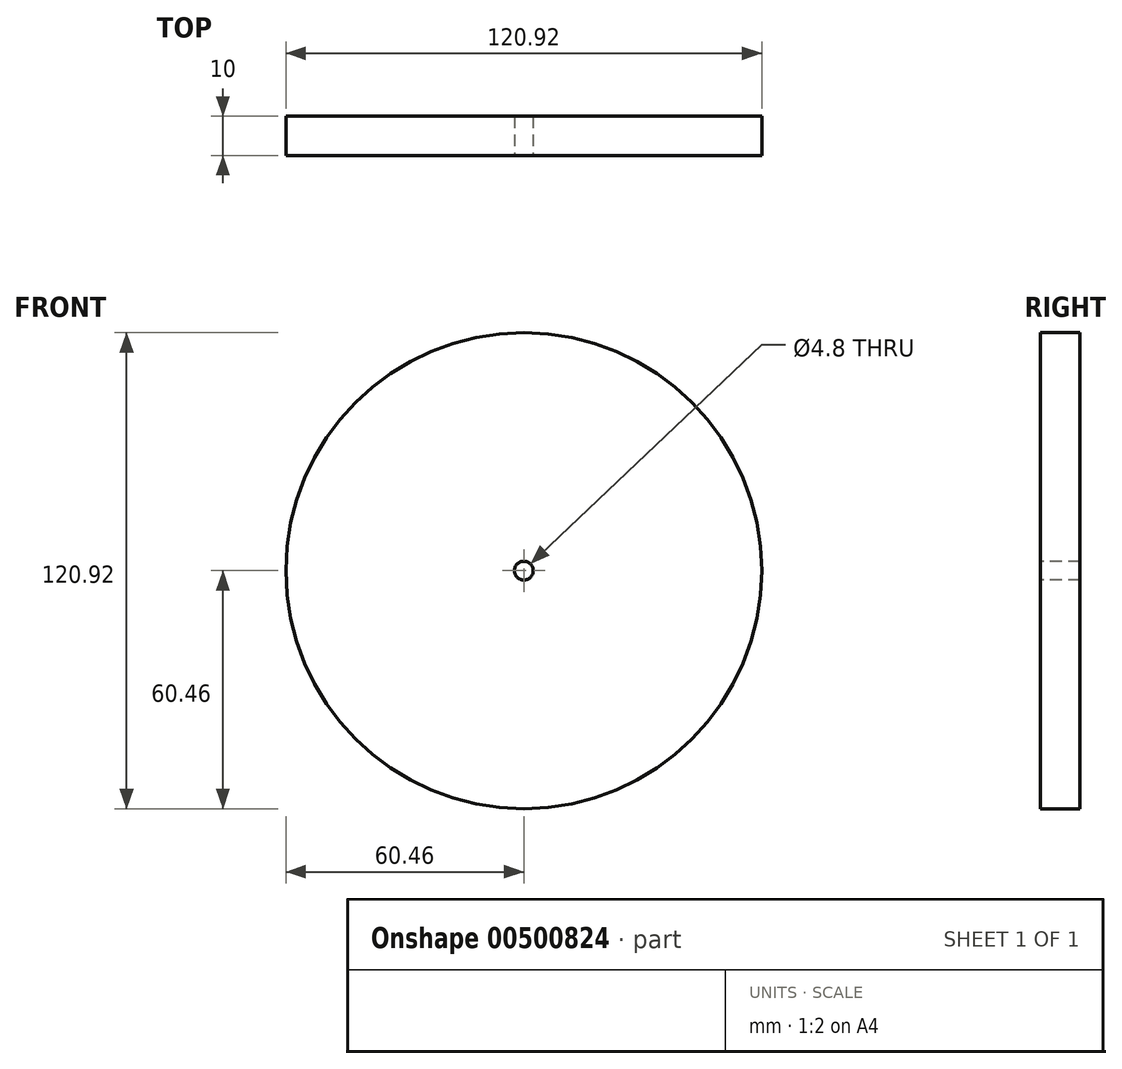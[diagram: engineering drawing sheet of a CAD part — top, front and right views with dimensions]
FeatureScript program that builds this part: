
annotation { "Feature Type Name" : "Feature", "Feature Type Description" : "" }
export const myFeature = defineFeature(function(context is Context, id is Id, definition is map)
    precondition{}
    {
        {
            var Q0;
            Q0=qCreatedBy(makeId("Front.planeOp"),FACE);
            var sketch = newSketch(context, id + "F0", { "sketchPlane" : qUnion([Q0])});
            skCircle(sketch, "E0", {"center": v(0, 0) * mm, "radius": 60.46 * mm});
            skSolve(sketch);
        }
        {
            var Q0;
            Q0=makeQuery(id+"F0.imprint","IMPRINT",FACE,{"disambiguationData":[TD([[makeQuery(id+"F0.imprint","IMPRINT",EDGE,{"derivedFrom":sQuery(id+"F0.wireOp",EDGE,"E0")}),1.0]])]});
            var sketch = newSketch(context, id + "F1", { "sketchPlane" : qUnion([Q0])});
            skCircle(sketch, "E1", {"center": v(0, 0) * mm, "radius": 2.4 * mm});
            skSolve(sketch);
        }
        {
            var Q0;
            Q0=makeQuery(id+"F0.imprint","IMPRINT",FACE,{"disambiguationData":[TD([[makeQuery(id+"F0.imprint","IMPRINT",EDGE,{"derivedFrom":sQuery(id+"F0.wireOp",EDGE,"E0")}),1.0]])]});
            extrude(context, id + "F2", {"entities" : qUnion([Q0]), "endBound" : BoundingType.SYMMETRIC, "depth" : 10 * mm});
        }
        {
            var Q0;
            Q0 = qSketchRegion(id + "F1", true);
            extrude(context, id + "F3", {"entities" : qUnion([Q0]), "operationType" : NewBodyOperationType.ADD, "endBound" : BoundingType.UP_TO_NEXT, "depth" : 25 * mm});
        }
        {
            var Q0;
            Q0 = qSketchRegion(id + "F1", true);
            extrude(context, id + "F4", {"entities" : qUnion([Q0]), "operationType" : NewBodyOperationType.REMOVE, "oppositeDirection" : true, "depth" : 25 * mm});
        }
        {
            var Q0;
            Q0 = qSketchRegion(id + "F1", true);
            extrude(context, id + "F5", {"entities" : qUnion([Q0]), "operationType" : NewBodyOperationType.REMOVE, "depth" : 25 * mm});
        }
    });
